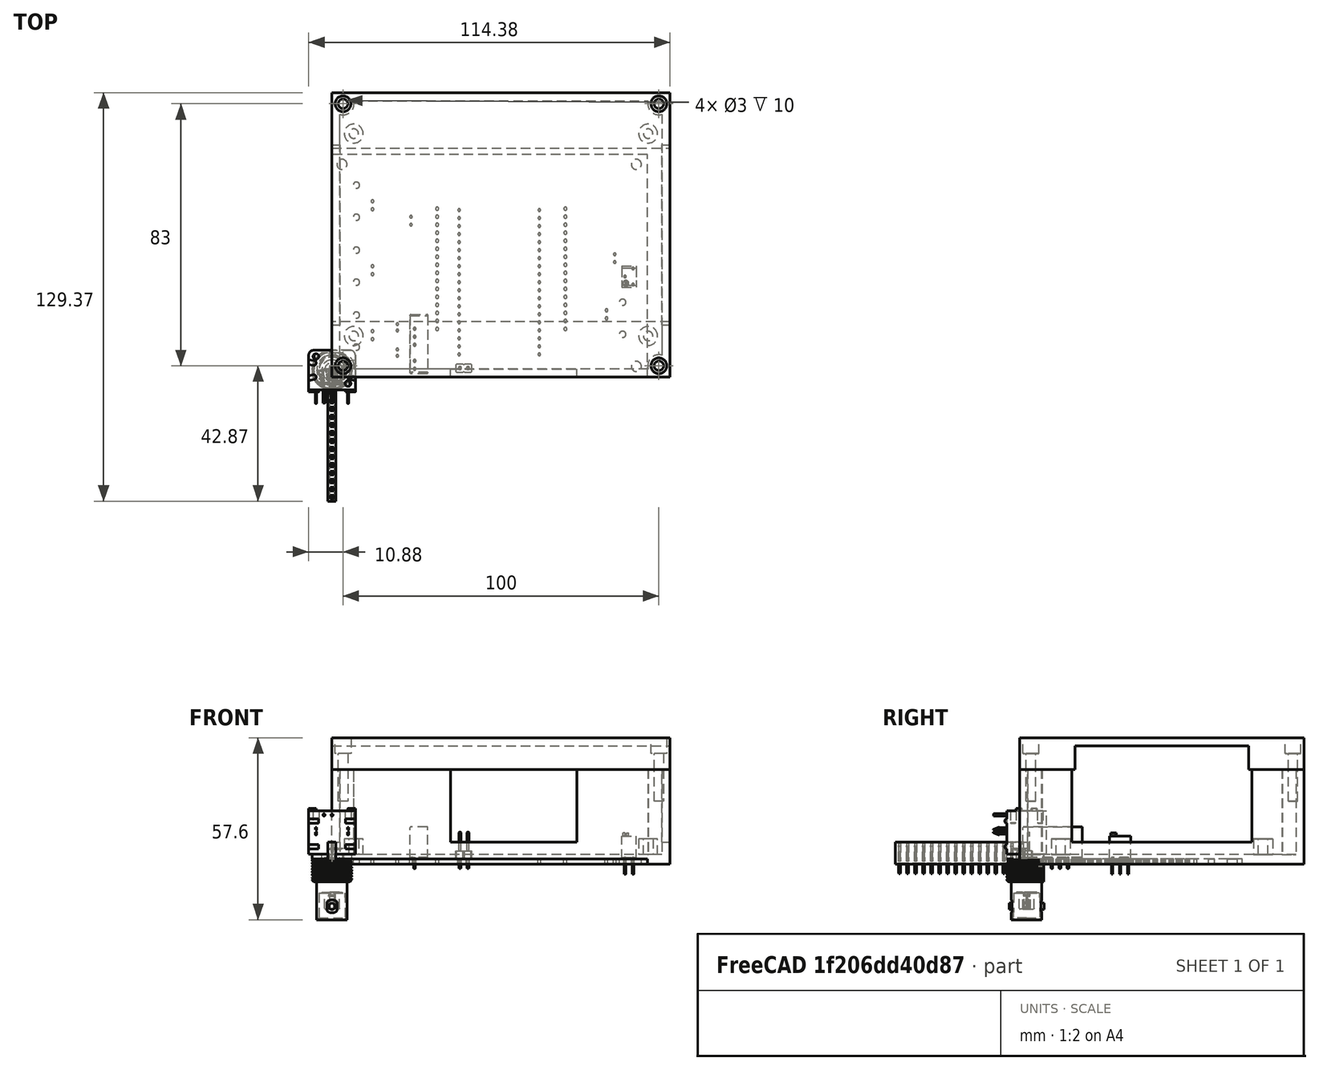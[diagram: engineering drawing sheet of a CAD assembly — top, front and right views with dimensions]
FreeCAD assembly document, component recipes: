
FREECAD ASSEMBLY — COMPONENT RECIPES ("moglabs-board-housing")

This assembly document has 10 components, labeled P0..P9 below (a component is one placed body or linked part). 2 of them carry a construction recipe — the FreeCAD feature program that regenerates the part from scratch, quoted from this document or its linked companion documents; the rest are supplied as boundary geometry only. No exploded tour is included for this assembly.
COMPONENT P0 — recipe-attached ("Base", modeled in this document).
Construction recipe (the document's own serialized feature program — sketch geometry with constraints, then the solid features built on it; lengths are millimeters unless a unit is written):

FEATURE [Sketcher::SketchObject] Sketch
  FullyConstrained = true
  MapMode = 5
  Support = -> [XY_Plane]
  sketch-geometry (4):
    g0: LineSegment StartX=0 StartY=0 StartZ=0 EndX=107 EndY=0 EndZ=0
    g1: LineSegment StartX=107 StartY=0 StartZ=0 EndX=107 EndY=90 EndZ=0
    g2: LineSegment StartX=107 StartY=90 StartZ=0 EndX=0 EndY=90 EndZ=0
    g3: LineSegment StartX=0 StartY=90 StartZ=0 EndX=0 EndY=0 EndZ=0
  constraints (11):
    c: Coincident(g0,g1)
    c: Coincident(g1,g2)
    c: Coincident(g2,g3)
    c: Coincident(g3,g0)
    c: Horizontal(g0)
    c: Horizontal(g2)
    c: Vertical(g1)
    c: Vertical(g3)
    c: Coincident(g0,g-1)
    c: DistanceX(g2,g2) = 107
    c: DistanceY(g1,g1) = 90
FEATURE [PartDesign::Pad] Pad
  Direction = (0,0,1)
  Length = 30
  Length2 = 10
  Profile = -> Sketch
  ReferenceAxis = -> Sketch [N_Axis]
  Type = 0
FEATURE [Sketcher::SketchObject] Sketch001
  ExternalGeometry = -> [Pad]
  FullyConstrained = true
  MapMode = 5
  Placement = pos=(0,0,30) rot=(0,0,1;0rad)
  Support = -> [Pad]
  sketch-geometry (7):
    g0: LineSegment StartX=2.5 StartY=87.5 StartZ=0 EndX=104.5 EndY=87.5 EndZ=0
    g1: LineSegment StartX=104.5 StartY=87.5 StartZ=0 EndX=104.5 EndY=2.5 EndZ=0
    g2: LineSegment StartX=104.5 StartY=2.5 StartZ=0 EndX=2.5 EndY=2.5 EndZ=0
    g3: LineSegment StartX=2.5 StartY=2.5 StartZ=0 EndX=2.5 EndY=87.5 EndZ=0
    g4: LineSegment StartX=0 StartY=90 StartZ=0 EndX=107 EndY=0 EndZ=0
    g5: LineSegment StartX=107 StartY=90 StartZ=0 EndX=0 EndY=0 EndZ=0
    g6: GeomPoint X=53.5 Y=45 Z=0
  constraints (19):
    c: Coincident(g0,g1)
    c: Coincident(g1,g2)
    c: Coincident(g2,g3)
    c: Coincident(g3,g0)
    c: Horizontal(g0)
    c: Horizontal(g2)
    c: Vertical(g1)
    c: Vertical(g3)
    c: Coincident(g4,g-6)
    c: Coincident(g4,g-5)
    c: Coincident(g5,g-5)
    c: Coincident(g5,g-6)
    c: PointOnObject(g6,g4)
    c: PointOnObject(g6,g5)
    c: Symmetric(g0,g1,g6)
    c: DistanceX(g4,g0) = 2.5
    c: DistanceY(g0,g4) = 2.5
    c: Distance(g0) = 102
    c: Distance(g3) = 85
FEATURE [PartDesign::Pocket] Pocket
  BaseFeature = -> Pad
  Direction = (0,0,-1)
  Length = 27
  Length2 = 5
  Profile = -> Sketch001
  ReferenceAxis = -> Sketch001 [N_Axis]
  Type = 0
FEATURE [Sketcher::SketchObject] Sketch002
  ExternalGeometry = -> [Pocket]
  FullyConstrained = true
  MapMode = 5
  Placement = pos=(0,0,3) rot=(0,0,1;0rad)
  Support = -> [Pocket]
  sketch-geometry (4):
    g0: Circle CenterX=3.5 CenterY=86.5 CenterZ=0 NormalX=0 NormalY=0 NormalZ=1 AngleXU=0 Radius=3.5
    g1: Circle CenterX=3.5 CenterY=3.5 CenterZ=0 NormalX=0 NormalY=0 NormalZ=1 AngleXU=0 Radius=3.5
    g2: Circle CenterX=103.5 CenterY=86.5 CenterZ=0 NormalX=0 NormalY=0 NormalZ=1 AngleXU=0 Radius=3.5
    g3: Circle CenterX=103.5 CenterY=3.5 CenterZ=0 NormalX=0 NormalY=0 NormalZ=1 AngleXU=0 Radius=3.5
  constraints (12):
    c: Radius(g0) = 3.5
    c: Tangent(g0,g-11)
    c: Tangent(g0,g-12)
    c: Equal(g1,g0)
    c: Tangent(g1,g-12)
    c: Tangent(g1,g-14)
    c: Equal(g2,g0)
    c: Equal(g3,g0)
    c: Tangent(g2,g-11)
    c: Tangent(g2,g-13)
    c: Tangent(g3,g-13)
    c: Tangent(g3,g-14)
FEATURE [PartDesign::Pad] Pad001
  BaseFeature = -> Pocket
  Direction = (0,0,1)
  Length = 27
  Length2 = 10
  Profile = -> Sketch002
  ReferenceAxis = -> Sketch002 [N_Axis]
  Type = 0
FEATURE [Sketcher::SketchObject] Sketch003
  ExternalGeometry = -> [Pad001]
  FullyConstrained = true
  MapMode = 5
  Placement = pos=(0,0,3) rot=(0,0,1;0rad)
  Support = -> [Pad001]
  sketch-geometry (11):
    g0: Circle CenterX=6.891 CenterY=77.04 CenterZ=0 NormalX=0 NormalY=0 NormalZ=1 AngleXU=0 Radius=3
    g1: Circle CenterX=6.891 CenterY=12.96 CenterZ=0 NormalX=0 NormalY=0 NormalZ=1 AngleXU=0 Radius=3
    g2: Circle CenterX=100.109 CenterY=77.04 CenterZ=0 NormalX=0 NormalY=0 NormalZ=1 AngleXU=0 Radius=3
    g3: Circle CenterX=100.109 CenterY=12.96 CenterZ=0 NormalX=0 NormalY=0 NormalZ=1 AngleXU=0 Radius=3
    g4: LineSegment StartX=6.891 StartY=77.04 StartZ=0 EndX=100.109 EndY=77.04 EndZ=0
    g5: LineSegment StartX=100.109 StartY=77.04 StartZ=0 EndX=100.109 EndY=12.96 EndZ=0
    g6: LineSegment StartX=100.109 StartY=12.96 StartZ=0 EndX=6.891 EndY=12.96 EndZ=0
    g7: LineSegment StartX=6.891 StartY=12.96 StartZ=0 EndX=6.891 EndY=77.04 EndZ=0
    g8: GeomPoint X=53.5 Y=45 Z=0
    g9: LineSegment StartX=0 StartY=90 StartZ=0 EndX=107 EndY=0 EndZ=0
    g10: LineSegment StartX=107 StartY=90 StartZ=0 EndX=0 EndY=0 EndZ=0
  constraints (25):
    c: Diameter(g0) = 6
    c: Equal(g1,g0)
    c: Equal(g2,g0)
    c: Equal(g3,g0)
    c: Coincident(g4,g5)
    c: Coincident(g5,g6)
    c: Coincident(g6,g7)
    c: Coincident(g7,g4)
    c: Horizontal(g4)
    c: Horizontal(g6)
    c: Vertical(g5)
    c: Vertical(g7)
    c: DistanceX(g4,g4) = 93.218
    c: DistanceY(g7,g7) = 64.08
    c: Coincident(g0,g4)
    c: Coincident(g1,g6)
    c: Coincident(g2,g4)
    c: Coincident(g3,g5)
    c: Symmetric(g0,g3,g8)
    c: Coincident(g9,g-10)
    c: Coincident(g9,g-8)
    c: Coincident(g10,g-9)
    c: Coincident(g10,g-11)
    c: PointOnObject(g8,g9)
    c: PointOnObject(g8,g10)
FEATURE [PartDesign::Pad] Pad002
  BaseFeature = -> Pad001
  Direction = (0,0,1)
  Length = 5
  Length2 = 10
  Profile = -> Sketch003
  ReferenceAxis = -> Sketch003 [N_Axis]
  Type = 0
FEATURE [Sketcher::SketchObject] Sketch004
  ExternalGeometry = -> [Pad002]
  FullyConstrained = true
  MapMode = 5
  Placement = pos=(0,0,8) rot=(0,0,1;0rad)
  Support = -> [Pad002]
  sketch-geometry (4):
    g0: Circle CenterX=6.891 CenterY=77.04 CenterZ=0 NormalX=0 NormalY=0 NormalZ=1 AngleXU=0 Radius=1.5
    g1: Circle CenterX=100.109 CenterY=77.04 CenterZ=0 NormalX=0 NormalY=0 NormalZ=1 AngleXU=0 Radius=1.5
    g2: Circle CenterX=100.109 CenterY=12.96 CenterZ=0 NormalX=0 NormalY=0 NormalZ=1 AngleXU=0 Radius=1.5
    g3: Circle CenterX=6.891 CenterY=12.96 CenterZ=0 NormalX=0 NormalY=0 NormalZ=1 AngleXU=0 Radius=1.5
  constraints (8):
    c: Coincident(g0,g-3)
    c: Diameter(g0) = 3
    c: Coincident(g1,g-4)
    c: Coincident(g2,g-5)
    c: Coincident(g3,g-6)
    c: Equal(g0,g3)
    c: Equal(g1,g0)
    c: Equal(g2,g0)
FEATURE [PartDesign::Pocket] Pocket001
  BaseFeature = -> Pad002
  Direction = (0,0,-1)
  Length = 5
  Length2 = 5
  Profile = -> Sketch004
  ReferenceAxis = -> Sketch004 [N_Axis]
  Type = 0
FEATURE [Sketcher::SketchObject] Sketch007
  ExternalGeometry = -> [Pad001]
  FullyConstrained = true
  MapMode = 5
  Placement = pos=(0,0,30) rot=(0,0,1;0rad)
  Support = -> [Pad001]
  sketch-geometry (4):
    g0: Circle CenterX=3.5 CenterY=86.5 CenterZ=0 NormalX=0 NormalY=0 NormalZ=1 AngleXU=0 Radius=1.5
    g1: Circle CenterX=103.5 CenterY=86.5 CenterZ=0 NormalX=0 NormalY=0 NormalZ=1 AngleXU=0 Radius=1.5
    g2: Circle CenterX=103.5 CenterY=3.5 CenterZ=0 NormalX=0 NormalY=0 NormalZ=1 AngleXU=0 Radius=1.5
    g3: Circle CenterX=3.5 CenterY=3.5 CenterZ=0 NormalX=0 NormalY=0 NormalZ=1 AngleXU=0 Radius=1.5
  constraints (8):
    c: Diameter(g0) = 3
    c: Equal(g3,g0)
    c: Equal(g1,g0)
    c: Equal(g2,g0)
    c: Coincident(g0,g-7)
    c: Coincident(g1,g-8)
    c: Coincident(g-10,g2)
    c: Coincident(g-9,g3)
FEATURE [PartDesign::Pocket] Pocket003
  BaseFeature = -> Pocket001
  Direction = (0,0,-1)
  Length = 10
  Length2 = 5
  Profile = -> Sketch007
  ReferenceAxis = -> Sketch007 [N_Axis]
  Type = 0
FEATURE [Sketcher::SketchObject] Sketch014
  ExternalGeometry = -> [Pocket003]
  FullyConstrained = true
  MapMode = 5
  Placement = pos=(0,0,0) rot=(0.57735,-0.57735,-0.57735;2.0944rad)
  sketch-geometry (5):
    g0: GeomPoint X=-45 Y=30 Z=0
    g1: LineSegment StartX=-73.5 StartY=30 StartZ=0 EndX=-16.5 EndY=30 EndZ=0
    g2: LineSegment StartX=-16.5 StartY=30 StartZ=0 EndX=-16.5 EndY=7 EndZ=0
    g3: LineSegment StartX=-16.5 StartY=7 StartZ=0 EndX=-73.5 EndY=7 EndZ=0
    g4: LineSegment StartX=-73.5 StartY=7 StartZ=0 EndX=-73.5 EndY=30 EndZ=0
  constraints (12):
    c: Coincident(g1,g2)
    c: Coincident(g2,g3)
    c: Coincident(g3,g4)
    c: Coincident(g4,g1)
    c: Horizontal(g1)
    c: Horizontal(g3)
    c: Vertical(g2)
    c: Vertical(g4)
    c: Symmetric(g1,g1,g0)
    c: DistanceX(g1,g1) = 57
    c: DistanceY(g4,g4) = 23
    c: Symmetric(g-3,g-3,g0)
FEATURE [PartDesign::Pocket] Pocket010
  BaseFeature = -> Pocket003
  Direction = (1,0,0)
  Length = 5
  Length2 = 5
  Profile = -> Sketch014
  ReferenceAxis = -> Sketch014 [N_Axis]
  Type = 1
FEATURE [Sketcher::SketchObject] Sketch015
  ExternalGeometry = -> [Pocket010]
  FullyConstrained = true
  MapMode = 5
  Placement = pos=(0,0,0) rot=(1,0,0;1.5708rad)
  Support = -> [Pocket010]
  sketch-geometry (4):
    g0: LineSegment StartX=37.5 StartY=30 StartZ=0 EndX=77.5 EndY=30 EndZ=0
    g1: LineSegment StartX=77.5 StartY=30 StartZ=0 EndX=77.5 EndY=7 EndZ=0
    g2: LineSegment StartX=77.5 StartY=7 StartZ=0 EndX=37.5 EndY=7 EndZ=0
    g3: LineSegment StartX=37.5 StartY=7 StartZ=0 EndX=37.5 EndY=30 EndZ=0
  constraints (12):
    c: Coincident(g0,g1)
    c: Coincident(g1,g2)
    c: Coincident(g2,g3)
    c: Coincident(g3,g0)
    c: Horizontal(g0)
    c: Horizontal(g2)
    c: Vertical(g1)
    c: Vertical(g3)
    c: PointOnObject(g0,g-3)
    c: DistanceX(g0,g0) = 40
    c: DistanceY(g3,g3) = 23
    c: DistanceX(g-3,g0) = 34
FEATURE [PartDesign::Pocket] Pocket011
  BaseFeature = -> Pocket010
  Direction = (0,1,-2e-16)
  Length = 5
  Length2 = 5
  Profile = -> Sketch015
  ReferenceAxis = -> Sketch015 [N_Axis]
  Type = 2
FEATURE [PartDesign::Body] Body  label="Base"
  Group = -> [Sketch,Pad,Sketch001,Pocket,Sketch002,Pad001,Sketch003,Pad002,Sketch004,Pocket001,Sketch007,Pocket003,Sketch014,Pocket010,Sketch015,Pocket011]
  Origin = -> Origin
  Tip = -> Pocket011
COMPONENT P1 — recipe-attached ("Top", modeled in this document).
Construction recipe (the document's own serialized feature program — sketch geometry with constraints, then the solid features built on it; lengths are millimeters unless a unit is written):

FEATURE [Sketcher::SketchObject] Sketch005
  FullyConstrained = true
  MapMode = 5
  Support = -> [XY_Plane001]
  sketch-geometry (4):
    g0: LineSegment StartX=0 StartY=0 StartZ=0 EndX=107 EndY=0 EndZ=0
    g1: LineSegment StartX=107 StartY=0 StartZ=0 EndX=107 EndY=90 EndZ=0
    g2: LineSegment StartX=107 StartY=90 StartZ=0 EndX=0 EndY=90 EndZ=0
    g3: LineSegment StartX=0 StartY=90 StartZ=0 EndX=0 EndY=0 EndZ=0
  constraints (11):
    c: Coincident(g0,g1)
    c: Coincident(g1,g2)
    c: Coincident(g2,g3)
    c: Coincident(g3,g0)
    c: Horizontal(g0)
    c: Horizontal(g2)
    c: Vertical(g1)
    c: Vertical(g3)
    c: Coincident(g0,g-1)
    c: DistanceX(g2,g2) = 107
    c: DistanceY(g1,g1) = 90
FEATURE [PartDesign::Pad] Pad003
  Direction = (0,0,1)
  Length = 10
  Length2 = 10
  Profile = -> Sketch005
  ReferenceAxis = -> Sketch005 [N_Axis]
  Type = 0
FEATURE [Sketcher::SketchObject] Sketch008
  ExternalGeometry = -> [Pad003]
  FullyConstrained = true
  MapMode = 5
  Placement = pos=(0,0,10) rot=(0,0,1;0rad)
  Support = -> [Pad003]
  sketch-geometry (1):
    g0: Circle CenterX=3.5 CenterY=86.5 CenterZ=0 NormalX=0 NormalY=0 NormalZ=1 AngleXU=0 Radius=2.5
  constraints (3):
    c: Diameter(g0) = 5
    c: DistanceY(g0,g-4) = 3.5
    c: DistanceX(g-4,g0) = 3.5
FEATURE [PartDesign::Pocket] Pocket004
  BaseFeature = -> Pad003
  Direction = (0,0,-1)
  Length = 5
  Length2 = 5
  Profile = -> Sketch008
  ReferenceAxis = -> Sketch008 [N_Axis]
  Type = 0
FEATURE [Sketcher::SketchObject] Sketch009
  ExternalGeometry = -> [Pocket004]
  FullyConstrained = true
  MapMode = 5
  Placement = pos=(0,0,5) rot=(0,0,1;0rad)
  Support = -> [Pocket004]
  sketch-geometry (1):
    g0: Circle CenterX=3.5 CenterY=86.5 CenterZ=0 NormalX=0 NormalY=0 NormalZ=1 AngleXU=0 Radius=1.5
  constraints (2):
    c: Coincident(g0,g-3)
    c: Diameter(g0) = 3
FEATURE [PartDesign::Pocket] Pocket005
  BaseFeature = -> Pocket004
  Direction = (0,0,-1)
  Length = 5
  Length2 = 5
  Profile = -> Sketch009
  ReferenceAxis = -> Sketch009 [N_Axis]
  Type = 1
FEATURE [PartDesign::LinearPattern] LinearPattern
  Direction = -> Sketch008 [H_Axis]
  Length = 100
  Occurrences = 2
FEATURE [PartDesign::LinearPattern] LinearPattern001
  Direction = -> Sketch008 [V_Axis]
  Length = 83
  Occurrences = 2
  Reversed = true
FEATURE [PartDesign::MultiTransform] MultiTransform
  BaseFeature = -> Pocket005
  Originals = -> [Pocket004]
  Transformations = -> [LinearPattern,LinearPattern001]
FEATURE [PartDesign::LinearPattern] LinearPattern002
  Direction = -> Sketch009 [H_Axis]
  Length = 100
  Occurrences = 2
FEATURE [PartDesign::LinearPattern] LinearPattern003
  Direction = -> Sketch009 [V_Axis]
  Length = 83
  Occurrences = 2
  Reversed = true
FEATURE [PartDesign::MultiTransform] MultiTransform001
  BaseFeature = -> MultiTransform
  Originals = -> [Pocket005]
  Transformations = -> [LinearPattern002,LinearPattern003]
FEATURE [Sketcher::SketchObject] Sketch012
  ExternalGeometry = -> [MultiTransform001]
  FullyConstrained = true
  MapMode = 5
  Placement = pos=(0,0,0) rot=(1,0,0;3.14159rad)
  Support = -> [MultiTransform001]
  sketch-geometry (8):
    g0: LineSegment StartX=0 StartY=0 StartZ=0 EndX=107 EndY=-90 EndZ=0
    g1: LineSegment StartX=107 StartY=0 StartZ=0 EndX=0 EndY=-90 EndZ=0
    g2: GeomPoint X=53.5 Y=-45 Z=0
    g3: LineSegment StartX=-1.5 StartY=-17.5 StartZ=0 EndX=-1.5 EndY=-72.5 EndZ=0
    g4: LineSegment StartX=-1.5 StartY=-72.5 StartZ=0 EndX=108.5 EndY=-72.5 EndZ=0
    g5: LineSegment StartX=108.5 StartY=-72.5 StartZ=0 EndX=108.5 EndY=-17.5 EndZ=0
    g6: LineSegment StartX=108.5 StartY=-17.5 StartZ=0 EndX=-1.5 EndY=-17.5 EndZ=0
    g7: GeomPoint X=53.5 Y=-45 Z=0
  constraints (18):
    c: Coincident(g0,g-1)
    c: Coincident(g0,g-5)
    c: Coincident(g1,g-3)
    c: Coincident(g1,g-4)
    c: PointOnObject(g2,g0)
    c: PointOnObject(g2,g1)
    c: Coincident(g3,g4)
    c: Coincident(g4,g5)
    c: Coincident(g5,g6)
    c: Coincident(g6,g3)
    c: Horizontal(g4)
    c: Horizontal(g6)
    c: Vertical(g3)
    c: Vertical(g5)
    c: Symmetric(g4,g3,g7)
    c: Coincident(g7,g2)
    c: DistanceX(g6,g6) = 110
    c: DistanceY(g3,g3) = 55
FEATURE [PartDesign::Pocket] Pocket008
  BaseFeature = -> MultiTransform001
  Direction = (0,0,1)
  Length = 7.5
  Length2 = 5
  Profile = -> Sketch012
  ReferenceAxis = -> Sketch012 [N_Axis]
  Type = 0
FEATURE [PartDesign::Body] Body001  label="Top"
  Group = -> [Sketch005,Pad003,Sketch008,Pocket004,Sketch009,Pocket005,MultiTransform,LinearPattern,LinearPattern001,MultiTransform001,LinearPattern002,LinearPattern003,Sketch012,Pocket008]
  Origin = -> Origin001
  Placement = pos=(0,0,30) rot=(0,0,1;0rad)
  Tip = -> Pocket008
COMPONENT P2 — geometry summary ("D_1206_3216Metric001"; no construction recipe available for this part):
  bounding box: 48.7 x 13.0 x 1.0 mm
  tessellated surface: 2,060 triangles
  volume: 25 mm^3 (4% of its bounding box)
  symmetry: mirror-symmetric across its z mid-plane
COMPONENT P3 — geometry summary ("C_1206_3216Metric001"; no construction recipe available for this part):
  bounding box: 67.6 x 42.3 x 1.6 mm
  tessellated surface: 940 triangles
  volume: 38 mm^3 (1% of its bounding box)
  symmetry: mirror-symmetric across its z mid-plane
COMPONENT P4 — geometry summary ("R_1206_3216Metric001"; no construction recipe available for this part):
  bounding box: 68.9 x 44.3 x 0.6 mm
  tessellated surface: 1,480 triangles
  volume: 26 mm^3 (2% of its bounding box)
  symmetry: mirror-symmetric across its z mid-plane
COMPONENT P5 — geometry summary ("SOIC-8_5.275x5.275mm_P1.27mm001"; no construction recipe available for this part):
  bounding box: 63.8 x 39.4 x 2.1 mm
  tessellated surface: 3,792 triangles
  volume: 157 mm^3 (3% of its bounding box)
COMPONENT P6 — geometry summary ("731000167001"; no construction recipe available for this part):
  bounding box: 140.3 x 55.9 x 16.8 mm
  tessellated surface: 99,708 triangles
  volume: 16064 mm^3 (12% of its bounding box)
COMPONENT P7 — geometry summary ("PinSocket_1x16_P2.54mm_Vertical001"; no construction recipe available for this part):
  bounding box: 43.2 x 40.6 x 10.1 mm
  tessellated surface: 3,384 triangles
  volume: 1359 mm^3 (8% of its bounding box)
  symmetry: 2-fold rotationally symmetric about the z axis; mirror-symmetric across its x mid-plane, y mid-plane
COMPONENT P8 — geometry summary ("C_Disc_D5.0mm_W2.5mm_P2.50mm001"; no construction recipe available for this part):
  bounding box: 67.0 x 16.8 x 7.1 mm
  tessellated surface: 10,288 triangles
  volume: 55 mm^3 (1% of its bounding box)
  symmetry: 2-fold rotationally symmetric about the z axis
COMPONENT P9 — geometry summary ("CP_Radial_D5.0mm_P2.00mm001"; no construction recipe available for this part):
  bounding box: 13.1 x 7.0 x 5.0 mm
  tessellated surface: 27,388 triangles
  volume: 186 mm^3 (41% of its bounding box)
  symmetry: 2-fold rotationally symmetric about the z axis; mirror-symmetric across its x mid-plane, y mid-plane
PROVENANCE & LICENSES
A FreeCAD (.FCStd) document from a public repository crawl; recipes are the document's own serialized feature recipes (and, for linked parts, companion documents' recipes).
License: gpl-3.0.
